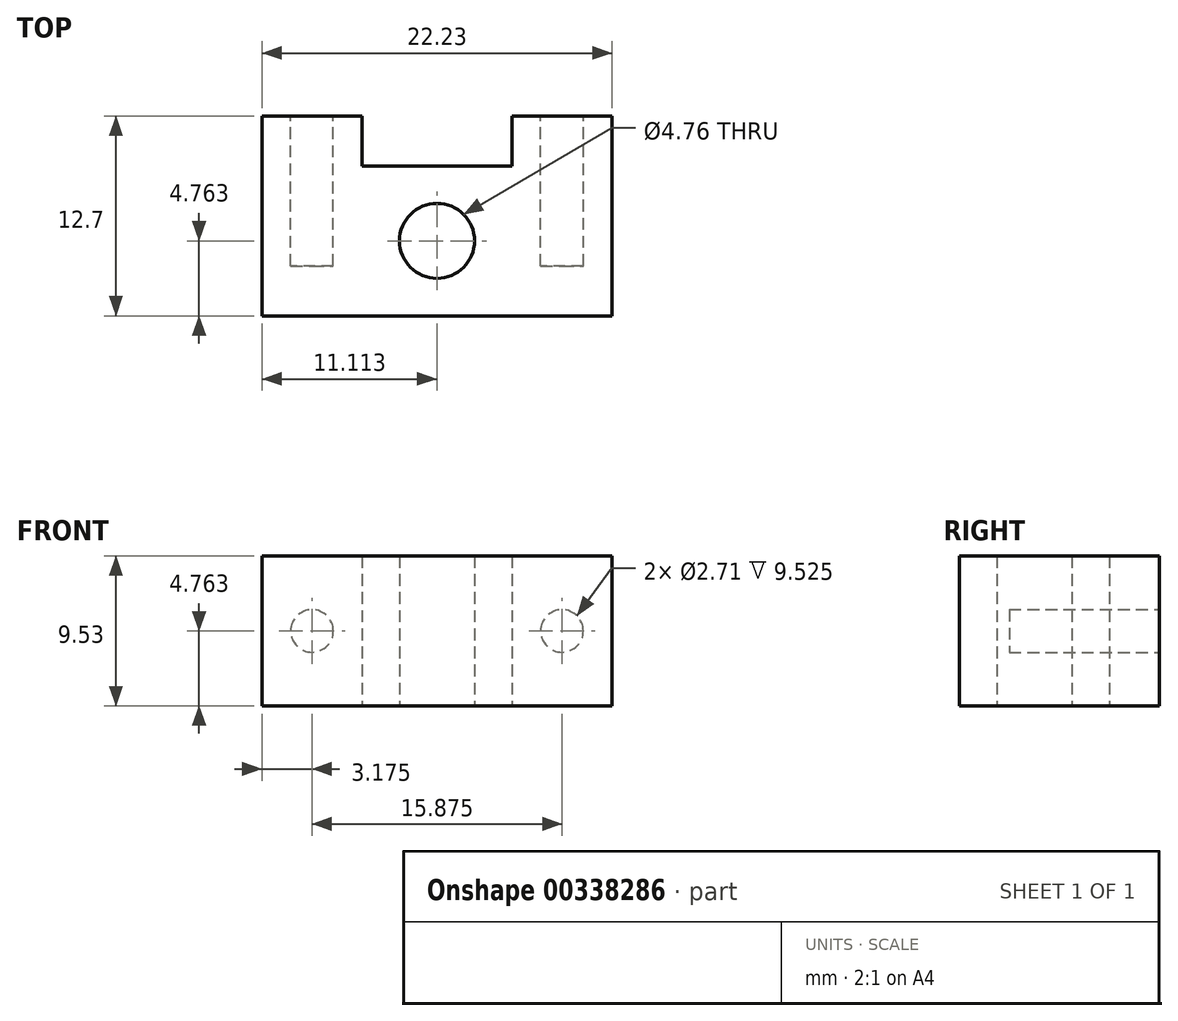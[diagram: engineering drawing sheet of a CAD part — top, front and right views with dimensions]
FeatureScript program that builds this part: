
annotation { "Feature Type Name" : "Feature", "Feature Type Description" : "" }
export const myFeature = defineFeature(function(context is Context, id is Id, definition is map)
    precondition{}
    {
        {
            var Q0;
            Q0=qCreatedBy(makeId("Top.planeOp"),FACE);
            var sketch = newSketch(context, id + "F0", { "sketchPlane" : qUnion([Q0])});
            skLineSegment(sketch, "E0.bottom", {"start": v(0, 0) * mm, "end": v(22.23, 0) * mm});
            skLineSegment(sketch, "E0.top", {"start": v(0, 12.7) * mm, "end": v(22.23, 12.7) * mm});
            skLineSegment(sketch, "E0.left", {"start": v(0, 0) * mm, "end": v(0, 12.7) * mm});
            skLineSegment(sketch, "E0.right", {"start": v(22.23, 0) * mm, "end": v(22.23, 12.7) * mm});
            skLineSegment(sketch, "E1", {"start": v(11.11, 0) * mm, "end": v(11.11, 4.76) * mm, "construction": true});
            skCircle(sketch, "E2", {"center": v(11.11, 4.76) * mm, "radius": 2.38 * mm});
            skSolve(sketch);
        }
        {
            var Q0;
            Q0 = qSketchRegion(id + "F0", true);
            extrude(context, id + "F1", {"entities" : qUnion([Q0]), "depth" : 9.52 * mm});
        }
        {
            var Q0;
            Q0=makeQuery(id+"F1.opExtrude","SWEPT_FACE",FACE,{"disambiguationData":[OSD([sQuery(id+"F0.wireOp",EDGE,"E0.top")])]});
            var sketch = newSketch(context, id + "F2", { "sketchPlane" : qUnion([Q0])});
            skLineSegment(sketch, "E3.bottom", {"start": v(0, 4.76) * mm, "end": v(-3.18, 4.76) * mm, "construction": true});
            skLineSegment(sketch, "E3.top", {"start": v(0, 9.53) * mm, "end": v(-3.18, 9.53) * mm, "construction": true});
            skLineSegment(sketch, "E3.left", {"start": v(0, 4.76) * mm, "end": v(0, 9.53) * mm, "construction": true});
            skLineSegment(sketch, "E3.right", {"start": v(-3.18, 4.76) * mm, "end": v(-3.18, 9.53) * mm, "construction": true});
            skLineSegment(sketch, "E4.bottom", {"start": v(-22.23, 4.76) * mm, "end": v(-19.05, 4.76) * mm, "construction": true});
            skLineSegment(sketch, "E4.top", {"start": v(-22.23, 9.53) * mm, "end": v(-19.05, 9.53) * mm, "construction": true});
            skLineSegment(sketch, "E4.left", {"start": v(-22.23, 4.76) * mm, "end": v(-22.23, 9.53) * mm, "construction": true});
            skLineSegment(sketch, "E4.right", {"start": v(-19.05, 4.76) * mm, "end": v(-19.05, 9.53) * mm, "construction": true});
            skCircle(sketch, "E5", {"center": v(-3.18, 4.76) * mm, "radius": 1.35 * mm});
            skCircle(sketch, "E6", {"center": v(-19.05, 4.76) * mm, "radius": 1.35 * mm});
            skSolve(sketch);
        }
        {
            var Q0;
            Q0 = qSketchRegion(id + "F2", true);
            extrude(context, id + "F3", {"entities" : qUnion([Q0]), "operationType" : NewBodyOperationType.REMOVE, "oppositeDirection" : true, "depth" : 9.52 * mm});
        }
        {
            var Q0;
            Q0=makeQuery(id+"F1.opExtrude","CAP_FACE",FACE,{"disambiguationData":[OSD([sQuery(id+"F0.wireOp",EDGE,"E0.bottom"),sQuery(id+"F0.wireOp",EDGE,"E0.top"),sQuery(id+"F0.wireOp",EDGE,"E0.left"),sQuery(id+"F0.wireOp",EDGE,"E0.right"),sQuery(id+"F0.wireOp",EDGE,"E2")])],"isStart":true});
            var sketch = newSketch(context, id + "F4", { "sketchPlane" : qUnion([Q0])});
            skLineSegment(sketch, "E7.bottom", {"start": v(15.88, -12.7) * mm, "end": v(6.35, -12.7) * mm});
            skLineSegment(sketch, "E7.top", {"start": v(15.88, -9.53) * mm, "end": v(6.35, -9.53) * mm});
            skLineSegment(sketch, "E7.left", {"start": v(15.88, -12.7) * mm, "end": v(15.88, -9.52) * mm});
            skLineSegment(sketch, "E7.right", {"start": v(6.35, -12.7) * mm, "end": v(6.35, -9.53) * mm});
            skLineSegment(sketch, "E8", {"start": v(11.11, -4.76) * mm, "end": v(11.11, -9.53) * mm, "construction": true});
            skLineSegment(sketch, "E9", {"start": v(11.11, -4.76) * mm, "end": v(11.11, 0) * mm, "construction": true});
            skLineSegment(sketch, "E10", {"start": v(11.11, -11.11) * mm, "end": v(15.88, -11.11) * mm, "construction": true});
            skLineSegment(sketch, "E11", {"start": v(11.11, -11.11) * mm, "end": v(6.35, -11.11) * mm, "construction": true});
            skSolve(sketch);
        }
        {
            var Q0;
            Q0 = qSketchRegion(id + "F4", true);
            var Q1;
            Q1=makeQuery(id+"F1.opExtrude","CAP_FACE",FACE,{"disambiguationData":[OSD([sQuery(id+"F0.wireOp",EDGE,"E0.bottom"),sQuery(id+"F0.wireOp",EDGE,"E0.top"),sQuery(id+"F0.wireOp",EDGE,"E0.left"),sQuery(id+"F0.wireOp",EDGE,"E0.right"),sQuery(id+"F0.wireOp",EDGE,"E2")])],"isStart":false});
            extrude(context, id + "F5", {"entities" : qUnion([Q0]), "operationType" : NewBodyOperationType.REMOVE, "endBound" : BoundingType.UP_TO_SURFACE, "oppositeDirection" : true, "endBoundEntityFace" : qUnion([Q1]), "depth" : 25.4 * mm});
        }
    });
